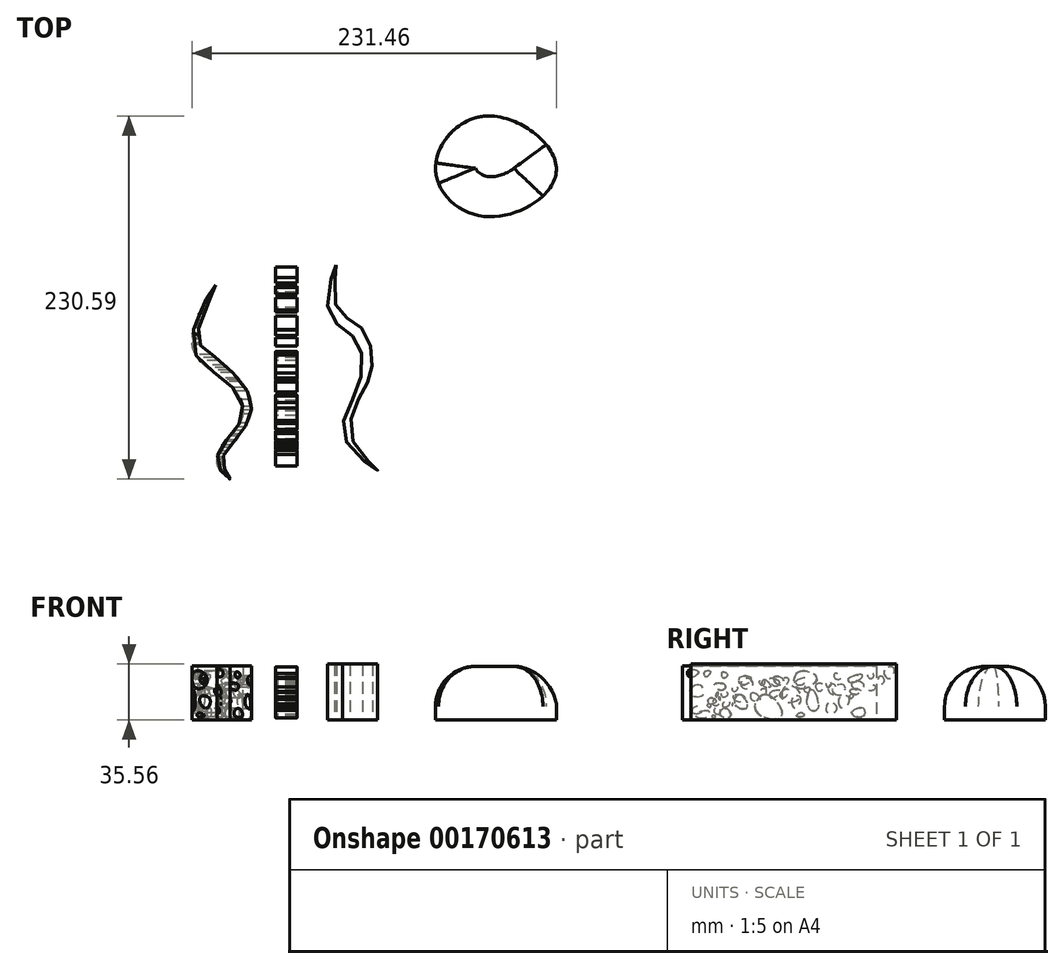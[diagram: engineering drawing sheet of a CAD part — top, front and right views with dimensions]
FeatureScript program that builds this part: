
annotation { "Feature Type Name" : "Feature", "Feature Type Description" : "" }
export const myFeature = defineFeature(function(context is Context, id is Id, definition is map)
    precondition{}
    {
        {
            var Q0;
            Q0=qCreatedBy(makeId("Top.planeOp"),FACE);
            var sketch = newSketch(context, id + "F0", { "sketchPlane" : qUnion([Q0])});
            skFitSpline(sketch, "E0", {"points": [v(-38.17, 55.88) * mm, v(-53.14, 19.85) * mm, v(-30.84, -5.8) * mm, v(-21.07, -27.48) * mm, v(-34.5, -46.72) * mm, v(-35.73, -61.08) * mm, v(-29.01, -67.18) * mm, v(-33.6, -58.33) * mm, v(-29.62, -47.33) * mm, v(-16.8, -29.01) * mm, v(-18.63, -10.38) * mm, v(-42.75, 13.44) * mm, v(-49.47, 25.04) * mm, v(-38.17, 55.88) * mm]});
            skSolve(sketch);
        }
        {
            var Q0;
            Q0 = qSketchRegion(id + "F0", true);
            extrude(context, id + "F1", {"entities" : qUnion([Q0]), "depth" : 34.3 * mm});
        }
        {
            var Q0;
            Q0=qCreatedBy(makeId("Right.planeOp"),FACE);
            var sketch = newSketch(context, id + "F2", { "sketchPlane" : qUnion([Q0])});
            skFitSpline(sketch, "E1", {"points": [v(-61.08, 4.89) * mm, v(-58.33, 8.55) * mm, v(-54.97, 5.2) * mm, v(-61.08, 4.89) * mm]});
            skFitSpline(sketch, "E2", {"points": [v(-49.46, 14) * mm, v(-50.68, 10.74) * mm, v(-45.79, 11.56) * mm, v(-49.46, 14) * mm]});
            skFitSpline(sketch, "E3", {"points": [v(-56.94, 22.3) * mm, v(-62.65, 16.87) * mm, v(-53.95, 16.05) * mm, v(-56.94, 22.3) * mm]});
            skFitSpline(sketch, "E4", {"points": [v(-30.96, 16.19) * mm, v(-33.81, 9.8) * mm, v(-26.2, 7.89) * mm, v(-30.96, 16.19) * mm]});
            skFitSpline(sketch, "E5", {"points": [v(-40.2, 22.3) * mm, v(-41.98, 18.9) * mm, v(-47.15, 22.3) * mm, v(-40.2, 22.3) * mm]});
            skFitSpline(sketch, "E6", {"points": [v(-40.2, 7.48) * mm, v(-43.34, 3.26) * mm, v(-36.67, 2.45) * mm, v(-40.2, 7.48) * mm]});
            skFitSpline(sketch, "E7", {"points": [v(-30.96, 26.93) * mm, v(-29.05, 22.3) * mm, v(-23.34, 26.25) * mm, v(-30.96, 26.93) * mm]});
            skFitSpline(sketch, "E8", {"points": [v(-53.27, 30.33) * mm, v(-52.31, 27.48) * mm, v(-49.46, 30.74) * mm, v(-53.27, 30.33) * mm]});
            skFitSpline(sketch, "E9", {"points": [v(-41.98, 30.33) * mm, v(-41.43, 26.8) * mm, v(-38.58, 28.7) * mm, v(-41.98, 30.33) * mm]});
            skFitSpline(sketch, "E10", {"points": [v(-62.79, 27.48) * mm, v(-56.94, 30.33) * mm, v(-63.2, 31.56) * mm, v(-62.79, 27.48) * mm]});
            skFitSpline(sketch, "E11", {"points": [v(-14.23, 16.19) * mm, v(-20.35, 5.57) * mm, v(-4.43, 2.3) * mm, v(-14.23, 16.19) * mm]});
            skFitSpline(sketch, "E12", {"points": [v(-15.04, 25.44) * mm, v(-16.4, 22.3) * mm, v(-11.37, 21.08) * mm, v(-15.04, 25.44) * mm]});
            skFitSpline(sketch, "E13", {"points": [v(14.62, 19.37) * mm, v(13.05, 7.48) * mm, v(18.89, 7.48) * mm, v(14.62, 19.37) * mm]});
            skFitSpline(sketch, "E14", {"points": [v(2.72, 14) * mm, v(4.3, 7.48) * mm, v(7.89, 14) * mm, v(2.72, 14) * mm]});
            skFitSpline(sketch, "E15", {"points": [v(-5.36, 16.19) * mm, v(-2.67, 14) * mm, v(0, 19.6) * mm, v(-5.36, 16.19) * mm]});
            skFitSpline(sketch, "E16", {"points": [v(-8.95, 27.23) * mm, v(-6.03, 22.3) * mm, v(-3.11, 25.43) * mm, v(-8.95, 27.23) * mm]});
            skFitSpline(sketch, "E17", {"points": [v(6.1, 30.33) * mm, v(6.32, 20.27) * mm, v(18.21, 26.33) * mm, v(6.1, 30.33) * mm]});
            skFitSpline(sketch, "E18", {"points": [v(9, 4.32) * mm, v(5.2, 2.75) * mm, v(9.68, 2.3) * mm, v(9, 4.32) * mm]});
            skFitSpline(sketch, "E19", {"points": [v(25.62, 10.84) * mm, v(31.01, 7.48) * mm, v(25.18, 4.32) * mm, v(25.62, 10.84) * mm]});
            skFitSpline(sketch, "E20", {"points": [v(25.4, 20.5) * mm, v(28.54, 16.19) * mm, v(29.67, 22.3) * mm, v(25.4, 20.5) * mm]});
            skFitSpline(sketch, "E21", {"points": [v(40.22, 4.32) * mm, v(47.4, 2.3) * mm, v(47.4, 7.48) * mm, v(40.22, 4.32) * mm]});
            skFitSpline(sketch, "E22", {"points": [v(39.4, 18.93) * mm, v(42.14, 16.19) * mm, v(45.8, 18.93) * mm, v(39.4, 18.93) * mm]});
            skFitSpline(sketch, "E23", {"points": [v(32.37, 14) * mm, v(34.5, 7.48) * mm, v(38.78, 14) * mm, v(32.37, 14) * mm]});
            skFitSpline(sketch, "E24", {"points": [v(37.92, 26.02) * mm, v(40.95, 23.71) * mm, v(47.25, 28.44) * mm, v(37.92, 26.02) * mm]});
            skFitSpline(sketch, "E25", {"points": [v(29.68, 29.53) * mm, v(29.68, 26.5) * mm, v(33.55, 26.62) * mm, v(29.68, 29.53) * mm]});
            skSolve(sketch);
        }
        {
            var Q0;
            Q0=makeQuery(id+"F2.imprint","IMPRINT",FACE,{"disambiguationData":[TD([[makeQuery(id+"F2.imprint","IMPRINT",EDGE,{"derivedFrom":sQuery(id+"F2.wireOp",EDGE,"E1")}),-1.0]])]});
            var Q1;
            Q1=makeQuery(id+"F2.imprint","IMPRINT",FACE,{"disambiguationData":[TD([[makeQuery(id+"F2.imprint","IMPRINT",EDGE,{"derivedFrom":sQuery(id+"F2.wireOp",EDGE,"E2")}),1.0]])]});
            var Q2;
            Q2=makeQuery(id+"F2.imprint","IMPRINT",FACE,{"disambiguationData":[TD([[makeQuery(id+"F2.imprint","IMPRINT",EDGE,{"derivedFrom":sQuery(id+"F2.wireOp",EDGE,"E3")}),1.0]])]});
            var Q3;
            Q3=makeQuery(id+"F2.imprint","IMPRINT",FACE,{"disambiguationData":[TD([[makeQuery(id+"F2.imprint","IMPRINT",EDGE,{"derivedFrom":sQuery(id+"F2.wireOp",EDGE,"E4")}),1.0]])]});
            var Q4;
            Q4=makeQuery(id+"F2.imprint","IMPRINT",FACE,{"disambiguationData":[TD([[makeQuery(id+"F2.imprint","IMPRINT",EDGE,{"derivedFrom":sQuery(id+"F2.wireOp",EDGE,"E5")}),-1.0]])]});
            var Q5;
            Q5=makeQuery(id+"F2.imprint","IMPRINT",FACE,{"disambiguationData":[TD([[makeQuery(id+"F2.imprint","IMPRINT",EDGE,{"derivedFrom":sQuery(id+"F2.wireOp",EDGE,"E6")}),1.0]])]});
            var Q6;
            Q6=makeQuery(id+"F2.imprint","IMPRINT",FACE,{"disambiguationData":[TD([[makeQuery(id+"F2.imprint","IMPRINT",EDGE,{"derivedFrom":sQuery(id+"F2.wireOp",EDGE,"E7")}),1.0]])]});
            var Q7;
            Q7=makeQuery(id+"F2.imprint","IMPRINT",FACE,{"disambiguationData":[TD([[makeQuery(id+"F2.imprint","IMPRINT",EDGE,{"derivedFrom":sQuery(id+"F2.wireOp",EDGE,"E8")}),1.0]])]});
            var Q8;
            Q8=makeQuery(id+"F2.imprint","IMPRINT",FACE,{"disambiguationData":[TD([[makeQuery(id+"F2.imprint","IMPRINT",EDGE,{"derivedFrom":sQuery(id+"F2.wireOp",EDGE,"E9")}),1.0]])]});
            var Q9;
            Q9=makeQuery(id+"F2.imprint","IMPRINT",FACE,{"disambiguationData":[TD([[makeQuery(id+"F2.imprint","IMPRINT",EDGE,{"derivedFrom":sQuery(id+"F2.wireOp",EDGE,"E10")}),1.0]])]});
            var Q10;
            Q10=makeQuery(id+"F2.imprint","IMPRINT",FACE,{"disambiguationData":[TD([[makeQuery(id+"F2.imprint","IMPRINT",EDGE,{"derivedFrom":sQuery(id+"F2.wireOp",EDGE,"E12")}),1.0]])]});
            var Q11;
            Q11=makeQuery(id+"F2.imprint","IMPRINT",FACE,{"disambiguationData":[TD([[makeQuery(id+"F2.imprint","IMPRINT",EDGE,{"derivedFrom":sQuery(id+"F2.wireOp",EDGE,"E13")}),1.0]])]});
            var Q12;
            Q12=makeQuery(id+"F2.imprint","IMPRINT",FACE,{"disambiguationData":[TD([[makeQuery(id+"F2.imprint","IMPRINT",EDGE,{"derivedFrom":sQuery(id+"F2.wireOp",EDGE,"E14")}),1.0]])]});
            var Q13;
            Q13=makeQuery(id+"F2.imprint","IMPRINT",FACE,{"disambiguationData":[TD([[makeQuery(id+"F2.imprint","IMPRINT",EDGE,{"derivedFrom":sQuery(id+"F2.wireOp",EDGE,"E15")}),1.0]])]});
            var Q14;
            Q14=makeQuery(id+"F2.imprint","IMPRINT",FACE,{"disambiguationData":[TD([[makeQuery(id+"F2.imprint","IMPRINT",EDGE,{"derivedFrom":sQuery(id+"F2.wireOp",EDGE,"E16")}),1.0]])]});
            var Q15;
            Q15=makeQuery(id+"F2.imprint","IMPRINT",FACE,{"disambiguationData":[TD([[makeQuery(id+"F2.imprint","IMPRINT",EDGE,{"derivedFrom":sQuery(id+"F2.wireOp",EDGE,"E17")}),1.0]])]});
            var Q16;
            Q16=makeQuery(id+"F2.imprint","IMPRINT",FACE,{"disambiguationData":[TD([[makeQuery(id+"F2.imprint","IMPRINT",EDGE,{"derivedFrom":sQuery(id+"F2.wireOp",EDGE,"E18")}),1.0]])]});
            var Q17;
            Q17=makeQuery(id+"F2.imprint","IMPRINT",FACE,{"disambiguationData":[TD([[makeQuery(id+"F2.imprint","IMPRINT",EDGE,{"derivedFrom":sQuery(id+"F2.wireOp",EDGE,"E19")}),-1.0]])]});
            var Q18;
            Q18=makeQuery(id+"F2.imprint","IMPRINT",FACE,{"disambiguationData":[TD([[makeQuery(id+"F2.imprint","IMPRINT",EDGE,{"derivedFrom":sQuery(id+"F2.wireOp",EDGE,"E20")}),1.0]])]});
            var Q19;
            Q19=makeQuery(id+"F2.imprint","IMPRINT",FACE,{"disambiguationData":[TD([[makeQuery(id+"F2.imprint","IMPRINT",EDGE,{"derivedFrom":sQuery(id+"F2.wireOp",EDGE,"E21")}),1.0]])]});
            var Q20;
            Q20=makeQuery(id+"F2.imprint","IMPRINT",FACE,{"disambiguationData":[TD([[makeQuery(id+"F2.imprint","IMPRINT",EDGE,{"derivedFrom":sQuery(id+"F2.wireOp",EDGE,"E22")}),1.0]])]});
            var Q21;
            Q21=makeQuery(id+"F2.imprint","IMPRINT",FACE,{"disambiguationData":[TD([[makeQuery(id+"F2.imprint","IMPRINT",EDGE,{"derivedFrom":sQuery(id+"F2.wireOp",EDGE,"E23")}),1.0]])]});
            var Q22;
            Q22=makeQuery(id+"F2.imprint","IMPRINT",FACE,{"disambiguationData":[TD([[makeQuery(id+"F2.imprint","IMPRINT",EDGE,{"derivedFrom":sQuery(id+"F2.wireOp",EDGE,"E24")}),1.0]])]});
            var Q23;
            Q23=makeQuery(id+"F2.imprint","IMPRINT",FACE,{"disambiguationData":[TD([[makeQuery(id+"F2.imprint","IMPRINT",EDGE,{"derivedFrom":sQuery(id+"F2.wireOp",EDGE,"E25")}),1.0]])]});
            var Q24;
            Q24=makeQuery(id+"F2.imprint","IMPRINT",FACE,{"disambiguationData":[TD([[makeQuery(id+"F2.imprint","IMPRINT",EDGE,{"derivedFrom":sQuery(id+"F2.wireOp",EDGE,"E11")}),1.0]])]});
            extrude(context, id + "F3", {"entities" : qUnion([Q0, Q1, Q2, Q3, Q4, Q5, Q6, Q7, Q8, Q9, Q10, Q11, Q12, Q13, Q14, Q15, Q16, Q17, Q18, Q19, Q20, Q21, Q22, Q23, Q24]), "operationType" : NewBodyOperationType.REMOVE, "oppositeDirection" : true, "depth" : 76.96 * mm});
        }
        {
            var Q0;
            Q0=qCreatedBy(makeId("Top.planeOp"),FACE);
            var sketch = newSketch(context, id + "F4", { "sketchPlane" : qUnion([Q0])});
            skFitSpline(sketch, "E26", {"points": [v(38.48, 68.71) * mm, v(33.6, 39.4) * mm, v(50.7, 21.68) * mm, v(52.22, -9.47) * mm, v(43.67, -41.53) * mm, v(64.74, -61.69) * mm, v(49.17, -43.06) * mm, v(54.05, -13.74) * mm, v(61.38, 5.2) * mm, v(53.75, 29.62) * mm, v(38.48, 42.45) * mm, v(38.48, 68.71) * mm]});
            skSolve(sketch);
        }
        {
            var Q0;
            Q0=makeQuery(id+"F4.imprint","IMPRINT",FACE,{"disambiguationData":[TD([[makeQuery(id+"F4.imprint","IMPRINT",EDGE,{"derivedFrom":sQuery(id+"F4.wireOp",EDGE,"E26")}),1.0]])]});
            extrude(context, id + "F5", {"entities" : qUnion([Q0]), "depth" : 35.56 * mm});
        }
        {
            var Q0;
            Q0=qCreatedBy(makeId("Right.planeOp"),FACE);
            var sketch = newSketch(context, id + "F6", { "sketchPlane" : qUnion([Q0])});
            skFitSpline(sketch, "E27", {"points": [v(-58.84, 2.78) * mm, v(-51.21, 2.05) * mm, v(-50.67, 5.69) * mm, v(-58.84, 2.78) * mm]});
            skFitSpline(sketch, "E28", {"points": [v(-47.22, 5.69) * mm, v(-43.95, 3.87) * mm, v(-43.77, 8.05) * mm, v(-47.22, 5.69) * mm]});
            skFitSpline(sketch, "E29", {"points": [v(-51.55, 9.47) * mm, v(-49.57, 8.11) * mm, v(-49.64, 9.88) * mm, v(-51.55, 9.47) * mm]});
            skFitSpline(sketch, "E30", {"points": [v(-47.22, 12.87) * mm, v(-47.22, 9.47) * mm, v(-43.86, 10.7) * mm, v(-47.22, 12.87) * mm]});
            skFitSpline(sketch, "E31", {"points": [v(-48.55, 2.54) * mm, v(-47.22, 1.24) * mm, v(-46.3, 2.33) * mm, v(-48.55, 2.54) * mm]});
            skFitSpline(sketch, "E32", {"points": [v(-41.94, 9.47) * mm, v(-39.36, 8.36) * mm, v(-36.92, 11.4) * mm, v(-39.5, 12.02) * mm, v(-41.94, 9.47) * mm]});
            skFitSpline(sketch, "E33", {"points": [v(-38.55, 17.31) * mm, v(-40.86, 14.26) * mm, v(-42.21, 17.31) * mm, v(-38.55, 17.31) * mm]});
            skFitSpline(sketch, "E34", {"points": [v(-44.32, 13.85) * mm, v(-43.16, 12.87) * mm, v(-43.37, 14.4) * mm, v(-44.32, 13.85) * mm]});
            skFitSpline(sketch, "E35", {"points": [v(-34.68, 15.48) * mm, v(-32.51, 11.75) * mm, v(-27.09, 13.85) * mm, v(-34.68, 15.48) * mm]});
            skFitSpline(sketch, "E36", {"points": [v(-35.84, 9.47) * mm, v(-35.3, 9.47) * mm, v(-35.36, 10.46) * mm, v(-35.84, 9.47) * mm]});
            skFitSpline(sketch, "E37", {"points": [v(-35.77, 20.23) * mm, v(-34.14, 18.06) * mm, v(-32.1, 20.57) * mm, v(-35.77, 20.23) * mm]});
            skFitSpline(sketch, "E38", {"points": [v(-45.94, 16.43) * mm, v(-45.6, 14.6) * mm, v(-44.32, 17.31) * mm, v(-45.94, 16.43) * mm]});
            skFitSpline(sketch, "E39", {"points": [v(-29.63, 24.36) * mm, v(-28.66, 20.23) * mm, v(-22.42, 21.88) * mm, v(-25.1, 26.3) * mm, v(-29.63, 24.36) * mm]});
            skFitSpline(sketch, "E40", {"points": [v(-22.85, 17.25) * mm, v(-23.28, 12.87) * mm, v(-17.57, 12.87) * mm, v(-22.85, 17.25) * mm]});
            skFitSpline(sketch, "E41", {"points": [v(-15.31, 16.28) * mm, v(-14.02, 19.19) * mm, v(-17.36, 18.97) * mm, v(-15.31, 16.28) * mm]});
            skFitSpline(sketch, "E42", {"points": [v(-18.22, 25) * mm, v(-17.25, 22.3) * mm, v(-14.66, 24.03) * mm, v(-18.22, 25) * mm]});
            skFitSpline(sketch, "E43", {"points": [v(-11.89, 16.55) * mm, v(-10.38, 13.96) * mm, v(-4.76, 18.06) * mm, v(-7.79, 18.7) * mm, v(-11.89, 16.55) * mm]});
            skFitSpline(sketch, "E44", {"points": [v(-5.84, 24.32) * mm, v(-8.43, 21.3) * mm, v(-11.89, 26.3) * mm, v(-5.84, 24.32) * mm]});
            skFitSpline(sketch, "E45", {"points": [v(-2.82, 20.22) * mm, v(-2.39, 11.8) * mm, v(7.76, 14.39) * mm, v(3.44, 21.08) * mm, v(-2.82, 20.22) * mm]});
            skFitSpline(sketch, "E46", {"points": [v(4.74, 24.32) * mm, v(7.76, 22.16) * mm, v(11.43, 26.3) * mm, v(4.74, 24.32) * mm]});
            skFitSpline(sketch, "E47", {"points": [v(9.92, 19.57) * mm, v(12.94, 17.63) * mm, v(12.94, 22.16) * mm, v(9.92, 19.57) * mm]});
            skFitSpline(sketch, "E48", {"points": [v(-2.82, 26.3) * mm, v(0, 26.3) * mm, v(-1.96, 22.16) * mm, v(-2.82, 26.3) * mm]});
            skFitSpline(sketch, "E49", {"points": [v(17.48, 22.16) * mm, v(19.85, 18.28) * mm, v(22.45, 22.16) * mm, v(17.48, 22.16) * mm]});
            skFitSpline(sketch, "E50", {"points": [v(27.84, 19.14) * mm, v(34.1, 16.12) * mm, v(35.19, 22.16) * mm, v(27.84, 19.14) * mm]});
            skFitSpline(sketch, "E51", {"points": [v(40.8, 24.32) * mm, v(42.53, 19.57) * mm, v(48.14, 22.16) * mm, v(40.8, 24.32) * mm]});
            skFitSpline(sketch, "E52", {"points": [v(50.3, 28.43) * mm, v(53.1, 26.3) * mm, v(54, 29.13) * mm, v(50.3, 28.43) * mm]});
            skFitSpline(sketch, "E53", {"points": [v(39.02, 15.58) * mm, v(39.93, 13.74) * mm, v(41.46, 15.99) * mm, v(39.02, 15.58) * mm]});
            skFitSpline(sketch, "E54", {"points": [v(24.24, 23.12) * mm, v(25.26, 20.78) * mm, v(27.4, 23.32) * mm, v(24.24, 23.12) * mm]});
            skFitSpline(sketch, "E55", {"points": [v(53.9, 22.16) * mm, v(55.32, 20.16) * mm, v(51.75, 18.74) * mm, v(53.9, 22.16) * mm]});
            skFitSpline(sketch, "E56", {"points": [v(58.38, 28.11) * mm, v(60.82, 24.32) * mm, v(57.97, 23.02) * mm, v(58.38, 28.11) * mm]});
            skFitSpline(sketch, "E57", {"points": [v(60.93, 31.37) * mm, v(64.29, 26.3) * mm, v(67.04, 32.9) * mm, v(60.93, 31.37) * mm]});
            skSolve(sketch);
        }
        {
            var Q0;
            Q0 = qSketchRegion(id + "F6", true);
            extrude(context, id + "F7", {"entities" : qUnion([Q0]), "depth" : 13.46 * mm});
        }
        {
            var Q0;
            Q0=qCreatedBy(makeId("Top.planeOp"),FACE);
            var sketch = newSketch(context, id + "F8", { "sketchPlane" : qUnion([Q0])});
            skFitSpline(sketch, "E58", {"points": [v(133.3, 163.28) * mm, v(101.58, 129) * mm, v(135.34, 99.33) * mm, v(178.32, 129.52) * mm, v(133.3, 163.28) * mm]});
            skSolve(sketch);
        }
        {
            var Q0;
            Q0 = qSketchRegion(id + "F8", true);
            var Q1;
            Q1=makeQuery(id+"F8.imprint","IMPRINT",FACE,{"disambiguationData":[TD([[makeQuery(id+"F8.imprint","IMPRINT",EDGE,{"derivedFrom":sQuery(id+"F8.wireOp",EDGE,"E58")}),1.0]])]});
            extrude(context, id + "F9", {"entities" : qUnion([Q0, Q1]), "depth" : 34.04 * mm});
        }
        {
            var Q0;
            Q0=makeQuery(id+"F9.opExtrude","CAP_EDGE",EDGE,{"disambiguationData":[OSD([sQuery(id+"F8.wireOp",EDGE,"E58")])],"isStart":false});
            fillet(context, id + "F10", {"entities" : qUnion([Q0]), "radius" : 25.4 * mm, "tangentPropagation" : true, "allowEdgeOverflow" : false});
        }
    });
